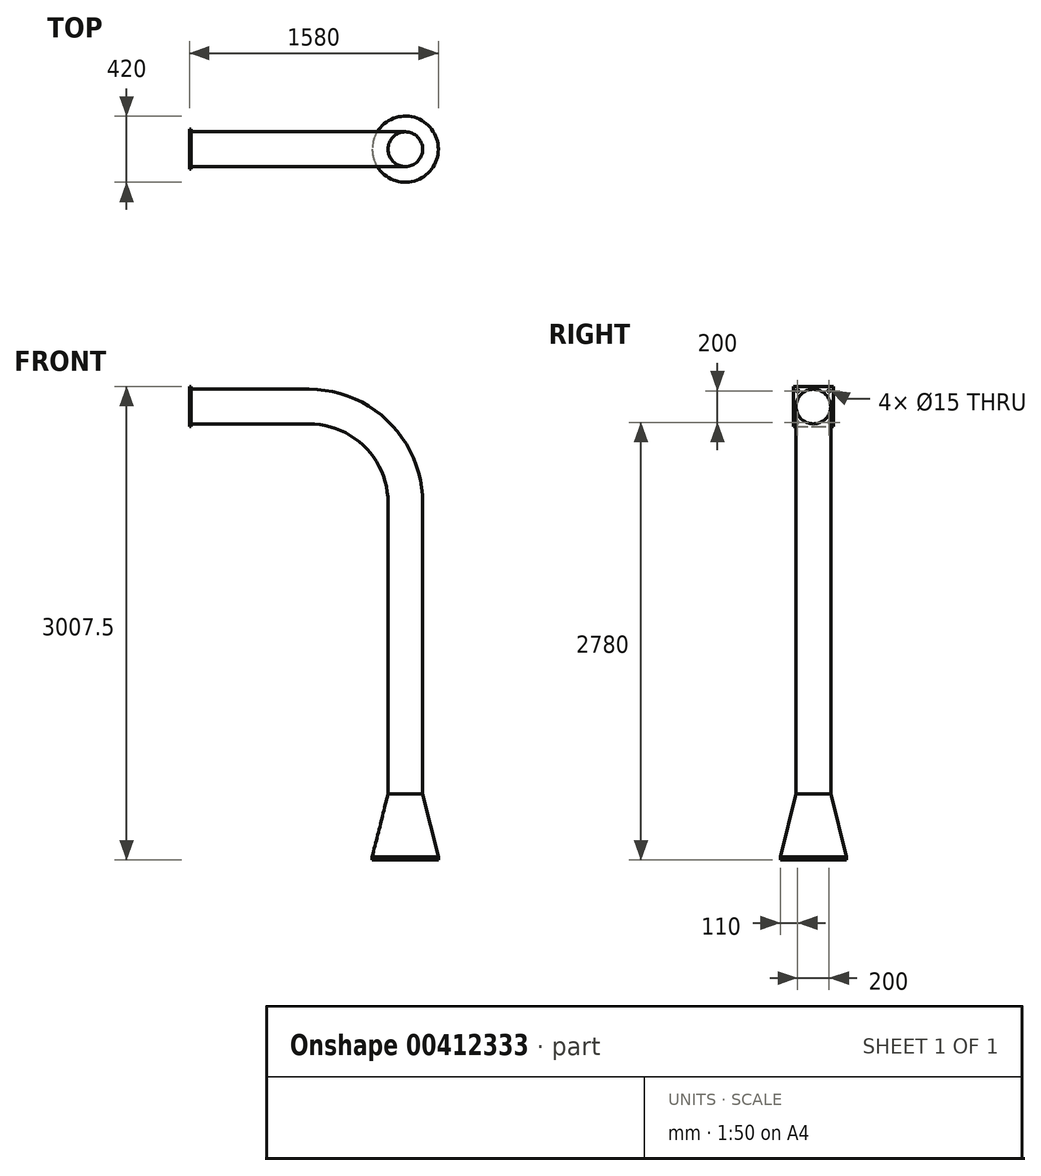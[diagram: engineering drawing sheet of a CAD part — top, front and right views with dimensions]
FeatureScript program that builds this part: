
annotation { "Feature Type Name" : "Feature", "Feature Type Description" : "" }
export const myFeature = defineFeature(function(context is Context, id is Id, definition is map)
    precondition{}
    {
        {
            var Q0;
            Q0=qCreatedBy(makeId("Right.planeOp"),FACE);
            var sketch = newSketch(context, id + "F0", { "sketchPlane" : qUnion([Q0])});
            skLineSegment(sketch, "E0.bottom", {"start": v(-32.32, 195.78) * mm, "end": v(167.68, 195.78) * mm, "construction": true});
            skLineSegment(sketch, "E0.top", {"start": v(-32.32, -4.22) * mm, "end": v(167.68, -4.22) * mm, "construction": true});
            skLineSegment(sketch, "E0.left", {"start": v(-32.32, 195.78) * mm, "end": v(-32.32, -4.22) * mm, "construction": true});
            skLineSegment(sketch, "E0.right", {"start": v(167.68, 195.78) * mm, "end": v(167.68, -4.22) * mm, "construction": true});
            skCircle(sketch, "E1", {"center": v(-32.32, 195.78) * mm, "radius": 7.5 * mm, "construction": true});
            skCircle(sketch, "E2", {"center": v(167.68, 195.78) * mm, "radius": 7.5 * mm, "construction": true});
            skCircle(sketch, "E3", {"center": v(167.68, -4.22) * mm, "radius": 7.5 * mm, "construction": true});
            skCircle(sketch, "E4", {"center": v(-32.32, -4.22) * mm, "radius": 7.5 * mm, "construction": true});
            skLineSegment(sketch, "E5", {"start": v(67.68, 195.78) * mm, "end": v(67.68, -4.22) * mm, "construction": true});
            skLineSegment(sketch, "E6", {"start": v(167.68, 95.78) * mm, "end": v(-32.32, 95.78) * mm, "construction": true});
            skPoint(sketch, "E7", {"position": v(67.68, 95.78) * mm});
            skLineSegment(sketch, "E8.bottom", {"start": v(-59.82, 223.28) * mm, "end": v(195.18, 223.28) * mm});
            skLineSegment(sketch, "E8.top", {"start": v(-59.82, -31.72) * mm, "end": v(195.18, -31.72) * mm});
            skLineSegment(sketch, "E8.left", {"start": v(-59.82, 223.28) * mm, "end": v(-59.82, -31.72) * mm});
            skLineSegment(sketch, "E8.right", {"start": v(195.18, 223.28) * mm, "end": v(195.18, -31.72) * mm});
            skSolve(sketch);
        }
        {
            var Q0;
            Q0 = qSketchRegion(id + "F0", true);
            extrude(context, id + "F1", {"entities" : qUnion([Q0]), "depth" : 10 * mm});
        }
        {
            var Q0;
            Q0=sQuery(id+"F0.wireOp",VERTEX,"E0.bottom.start");
            var Q1;
            Q1=sQuery(id+"F0.wireOp",VERTEX,"E0.right.start");
            var Q2;
            Q2=sQuery(id+"F0.wireOp",VERTEX,"E0.right.end");
            var Q3;
            Q3=sQuery(id+"F0.wireOp",VERTEX,"E4.center");
            var Q4;
            Q4=makeQuery(id+"F1.opExtrude","SWEPT_BODY",BODY,{"disambiguationData":[OSD([sQuery(id+"F0.wireOp",EDGE,"E8.bottom"),sQuery(id+"F0.wireOp",EDGE,"E8.top"),sQuery(id+"F0.wireOp",EDGE,"E8.left"),sQuery(id+"F0.wireOp",EDGE,"E8.right")])]});
            hole(context, id + "F2", {"style" : HoleStyle.SIMPLE, "endStyle" : HoleEndStyle.THROUGH, "oppositeDirection" : true, "holeDiameter" : 15 * mm, "isTappedThrough" : true, "tappedDepth" : 12 * mm, "tapClearance" : 3, "startFromSketch" : true, "locations" : qUnion([Q0, Q1, Q2, Q3]), "scope" : qUnion([Q4])});
        }
        {
            var Q0;
            Q0=makeQuery(id+"F1.opExtrude","CAP_FACE",FACE,{"disambiguationData":[OSD([sQuery(id+"F0.wireOp",EDGE,"E8.bottom"),sQuery(id+"F0.wireOp",EDGE,"E8.top"),sQuery(id+"F0.wireOp",EDGE,"E8.left"),sQuery(id+"F0.wireOp",EDGE,"E8.right")])],"isStart":false});
            var sketch = newSketch(context, id + "F3", { "sketchPlane" : qUnion([Q0])});
            skLineSegment(sketch, "E9", {"start": v(67.68, 223.28) * mm, "end": v(67.68, -31.72) * mm, "construction": true});
            skLineSegment(sketch, "E10", {"start": v(-59.82, 95.78) * mm, "end": v(195.18, 95.78) * mm, "construction": true});
            skPoint(sketch, "E11", {"position": v(67.68, 95.78) * mm});
            skCircle(sketch, "E12", {"center": v(67.68, 95.78) * mm, "radius": 110 * mm});
            skSolve(sketch);
        }
        {
            var Q0;
            Q0 = qSketchRegion(id + "F3", true);
            extrude(context, id + "F4", {"entities" : qUnion([Q0]), "operationType" : NewBodyOperationType.ADD, "depth" : 750 * mm});
        }
        {
            var Q0;
            Q0=makeQuery(id+"F4.opExtrude","CAP_FACE",FACE,{"disambiguationData":[OSD([sQuery(id+"F3.wireOp",EDGE,"E12")])],"isStart":false});
            var sketch = newSketch(context, id + "F5", { "sketchPlane" : qUnion([Q0])});
            skCircle(sketch, "E13", {"center": v(67.68, 95.78) * mm, "radius": 110 * mm});
            skLineSegment(sketch, "E14", {"start": v(-248.54, -514.22) * mm, "end": v(437.01, -514.22) * mm, "construction": true});
            skSolve(sketch);
        }
        {
            var Q0;
            Q0=makeQuery(id+"F5.imprint","IMPRINT",FACE,{"disambiguationData":[TD([[makeQuery(id+"F5.imprint","IMPRINT",EDGE,{"derivedFrom":sQuery(id+"F5.wireOp",EDGE,"E13")}),1.0]])]});
            var Q1;
            Q1=sQuery(id+"F5.wireOp",EDGE,"E14");
            revolve(context, id + "F6", {"operationType" : NewBodyOperationType.ADD, "entities" : qUnion([Q0]), "axis" : qUnion([Q1]), "revolveType" : RevolveType.ONE_DIRECTION, "angle" : 90 * degree});
        }
        {
            var Q0;
            Q0=makeQuery(id+"F6.opRevolve","CAP_FACE",FACE,{"disambiguationData":[OSD([sQuery(id+"F5.wireOp",EDGE,"Tuodn0gR-hCRY-UiNz-9GZa-srnmXqNyj3O1"),sQuery(id+"F5.wireOp",EDGE,"E13")])],"isStart":false});
            extrude(context, id + "F7", {"entities" : qUnion([Q0]), "operationType" : NewBodyOperationType.ADD, "depth" : 1850 * mm});
        }
        {
            var Q0;
            Q0=makeQuery(id+"F7.opExtrude","CAP_FACE",FACE,{"disambiguationData":[OSD([sQuery(id+"F5.wireOp",EDGE,"Tuodn0gR-hCRY-UiNz-9GZa-srnmXqNyj3O1"),sQuery(id+"F5.wireOp",EDGE,"E13")])],"isStart":false});
            cPlane(context, id + "F8", {"entities" : qUnion([Q0]), "cplaneType" : CPlaneType.OFFSET, "offset" : 400 * mm, "width" : 150 * mm, "height" : 150 * mm});
        }
        {
            var Q0;
            Q0=qCreatedBy(id+"F8.planeOp",FACE);
            var sketch = newSketch(context, id + "F9", { "sketchPlane" : qUnion([Q0])});
            skCircle(sketch, "E15", {"center": v(1370, -67.68) * mm, "radius": 210 * mm});
            skSolve(sketch);
        }
        {
            var Q0;
            Q0 = qSketchRegion(id + "F9", true);
            extrude(context, id + "F10", {"entities" : qUnion([Q0]), "depth" : 20 * mm});
        }
        {
            var Q0;
            Q0=makeQuery(id+"F10.opExtrude","CAP_FACE",FACE,{"disambiguationData":[OSD([sQuery(id+"F9.wireOp",EDGE,"E15")])],"isStart":true});
            var Q1;
            Q1=makeQuery(id+"F7.opExtrude","CAP_FACE",FACE,{"disambiguationData":[OSD([sQuery(id+"F5.wireOp",EDGE,"E13")])],"isStart":false});
            loft(context, id + "F11", {"sheetProfilesArray" : [{ "sheetProfileEntities" : qUnion([Q0]) }, { "sheetProfileEntities" : qUnion([Q1]) }]});
        }
    });
